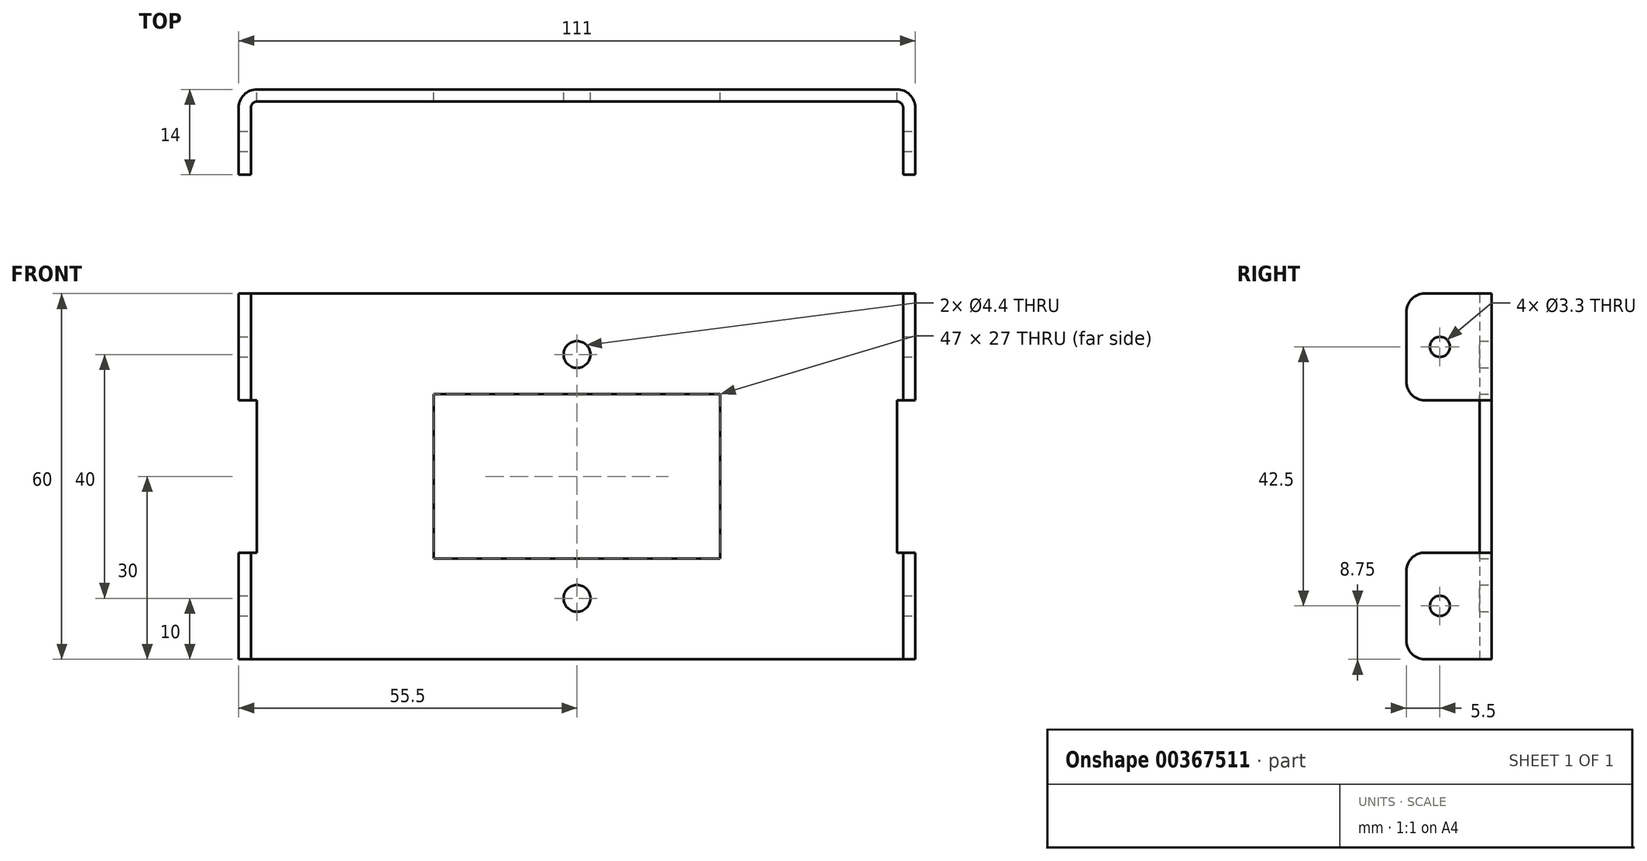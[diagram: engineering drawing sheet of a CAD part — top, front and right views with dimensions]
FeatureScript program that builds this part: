
annotation { "Feature Type Name" : "Feature", "Feature Type Description" : "" }
export const myFeature = defineFeature(function(context is Context, id is Id, definition is map)
    precondition{}
    {
        {
            var Q0;
            Q0=qCreatedBy(makeId("Top.planeOp"),FACE);
            var sketch = newSketch(context, id + "F0", { "sketchPlane" : qUnion([Q0])});
            skLineSegment(sketch, "E0", {"start": v(52.5, 0) * mm, "end": v(-52.5, 0) * mm});
            skLineSegment(sketch, "E1", {"start": v(-53.5, -1) * mm, "end": v(-53.5, -12) * mm});
            skLineSegment(sketch, "E2", {"start": v(53.5, -1) * mm, "end": v(53.5, -12) * mm});
            skPoint(sketch, "E3", {"position": v(0, 0) * mm});
            skPoint(sketch, "E4.visualSharp", {"position": v(-53.5, 0) * mm});
            skArc(sketch, "E4.filletArc", {"start": v(-52.5, 0) * mm, "mid": v(-53.2, -0.3) * mm, "end": v(-53.5, -1) * mm});
            skPoint(sketch, "E5.visualSharp", {"position": v(53.5, 0) * mm});
            skArc(sketch, "E5.filletArc", {"start": v(53.5, -1) * mm, "mid": v(53.2, -0.3) * mm, "end": v(52.5, 0) * mm});
            skLineSegment(sketch, "E6.0", {"start": v(-55.5, -1) * mm, "end": v(-55.5, -12) * mm});
            skLineSegment(sketch, "E6.1", {"start": v(55.5, -1) * mm, "end": v(55.5, -12) * mm});
            skArc(sketch, "E6.2", {"start": v(55.5, -1) * mm, "mid": v(54.62, 1.12) * mm, "end": v(52.5, 2) * mm});
            skLineSegment(sketch, "E6.3", {"start": v(52.5, 2) * mm, "end": v(-52.5, 2) * mm});
            skArc(sketch, "E6.4", {"start": v(-52.5, 2) * mm, "mid": v(-54.62, 1.12) * mm, "end": v(-55.5, -1) * mm});
            skLineSegment(sketch, "E7", {"start": v(-55.5, -12) * mm, "end": v(-53.5, -12) * mm});
            skLineSegment(sketch, "E8", {"start": v(53.5, -12) * mm, "end": v(55.5, -12) * mm});
            skSolve(sketch);
        }
        {
            var Q0;
            Q0=makeQuery(id+"F0.imprint","IMPRINT",FACE,{"disambiguationData":[TD([[makeQuery(id+"F0.imprint","IMPRINT",EDGE,{"derivedFrom":sQuery(id+"F0.wireOp",EDGE,"E0")}),-1.0]])]});
            extrude(context, id + "F1", {"entities" : qUnion([Q0]), "endBound" : BoundingType.SYMMETRIC, "depth" : 60 * mm});
        }
        {
            var Q0;
            Q0=makeQuery(id+"F1.opExtrude","SWEPT_FACE",FACE,{"disambiguationData":[OSD([sQuery(id+"F0.wireOp",EDGE,"E6.3")])]});
            var sketch = newSketch(context, id + "F2", { "sketchPlane" : qUnion([Q0])});
            skLineSegment(sketch, "E9.0", {"start": v(-55.5, 30) * mm, "end": v(-55.5, -30) * mm, "construction": true});
            skLineSegment(sketch, "E10.0", {"start": v(55.5, 30) * mm, "end": v(55.5, -30) * mm, "construction": true});
            skLineSegment(sketch, "E11.bottom", {"start": v(-55.5, 12.5) * mm, "end": v(-52.5, 12.5) * mm});
            skLineSegment(sketch, "E11.top", {"start": v(-55.5, -12.5) * mm, "end": v(-52.5, -12.5) * mm});
            skLineSegment(sketch, "E11.left", {"start": v(-55.5, 12.5) * mm, "end": v(-55.5, -12.5) * mm});
            skLineSegment(sketch, "E11.right", {"start": v(-52.5, 12.5) * mm, "end": v(-52.5, -12.5) * mm});
            skPoint(sketch, "E12", {"position": v(-52.5, 0) * mm});
            skLineSegment(sketch, "E13", {"start": v(0, 0) * mm, "end": v(0, 30) * mm, "construction": true});
            skLineSegment(sketch, "E14.MirrorCS", {"start": v(55.5, 12.5) * mm, "end": v(52.5, 12.5) * mm});
            skLineSegment(sketch, "E15.MirrorCS", {"start": v(55.5, -12.5) * mm, "end": v(52.5, -12.5) * mm});
            skPoint(sketch, "E16.MirrorP", {"position": v(52.5, 0) * mm});
            skLineSegment(sketch, "E17.MirrorCS", {"start": v(55.5, 12.5) * mm, "end": v(55.5, -12.5) * mm});
            skLineSegment(sketch, "E18.MirrorCS", {"start": v(52.5, 12.5) * mm, "end": v(52.5, -12.5) * mm});
            skLineSegment(sketch, "E19.bottom", {"start": v(23.5, 13.5) * mm, "end": v(-23.5, 13.5) * mm});
            skLineSegment(sketch, "E19.top", {"start": v(23.5, -13.5) * mm, "end": v(-23.5, -13.5) * mm});
            skLineSegment(sketch, "E19.left", {"start": v(23.5, 13.5) * mm, "end": v(23.5, -13.5) * mm});
            skLineSegment(sketch, "E19.right", {"start": v(-23.5, 13.5) * mm, "end": v(-23.5, -13.5) * mm});
            skPoint(sketch, "E19.middle", {"position": v(0, 0) * mm});
            skPoint(sketch, "E20", {"position": v(0, 20) * mm});
            skLineSegment(sketch, "E21", {"start": v(0, 0) * mm, "end": v(23.5, 0) * mm, "construction": true});
            skPoint(sketch, "E22", {"position": v(0, -20) * mm});
            skSolve(sketch);
        }
        {
            var Q0;
            Q0=makeQuery(id+"F2.imprint","IMPRINT",FACE,{"disambiguationData":[TD([[makeQuery(id+"F2.imprint","IMPRINT",EDGE,{"derivedFrom":sQuery(id+"F2.wireOp",EDGE,"E11.bottom")}),-1.0]])]});
            var Q1;
            Q1=makeQuery(id+"F2.imprint","IMPRINT",FACE,{"disambiguationData":[TD([[makeQuery(id+"F2.imprint","IMPRINT",EDGE,{"derivedFrom":sQuery(id+"F2.wireOp",EDGE,"E14.MirrorCS")}),1.0]])]});
            var Q2;
            Q2=makeQuery(id+"F2.imprint","IMPRINT",FACE,{"disambiguationData":[TD([[makeQuery(id+"F2.imprint","IMPRINT",EDGE,{"derivedFrom":sQuery(id+"F2.wireOp",EDGE,"E19.bottom")}),1.0]])]});
            extrude(context, id + "F3", {"entities" : qUnion([Q0, Q1, Q2]), "operationType" : NewBodyOperationType.REMOVE, "endBound" : BoundingType.THROUGH_ALL, "oppositeDirection" : true, "depth" : 25 * mm});
        }
        {
            var Q0;
            Q0=sQuery(id+"F2.wireOp",VERTEX,"E20");
            var Q1;
            Q1=sQuery(id+"F2.wireOp",VERTEX,"E22");
            var Q2;
            Q2=makeQuery(id+"F1.opExtrude","SWEPT_BODY",BODY,{"disambiguationData":[OSD([sQuery(id+"F0.wireOp",EDGE,"E0"),sQuery(id+"F0.wireOp",EDGE,"E1"),sQuery(id+"F0.wireOp",EDGE,"E2"),sQuery(id+"F0.wireOp",EDGE,"E4.filletArc"),sQuery(id+"F0.wireOp",EDGE,"E5.filletArc"),sQuery(id+"F0.wireOp",EDGE,"E6.0"),sQuery(id+"F0.wireOp",EDGE,"E6.1"),sQuery(id+"F0.wireOp",EDGE,"E6.2"),sQuery(id+"F0.wireOp",EDGE,"E6.3"),sQuery(id+"F0.wireOp",EDGE,"E6.4"),sQuery(id+"F0.wireOp",EDGE,"E7"),sQuery(id+"F0.wireOp",EDGE,"E8")])]});
            hole(context, id + "F4", {"style" : HoleStyle.SIMPLE, "endStyle" : HoleEndStyle.THROUGH, "standardTappedOrClearance" : lookupTablePath({ "standard" : "ISO", "fit" : "Normal", "size" : "M4", "type" : "Clearance" }), "standardBlindInLast" : lookupTablePath({ "fit" : "Standard", "standard" : "ISO", "size" : "M4", "type" : "Clearance" }), "holeDiameter" : 4.4 * mm, "tappedDepth" : 12 * mm, "tapClearance" : 3, "locations" : qUnion([Q0, Q1]), "scope" : qUnion([Q2])});
        }
        {
            var Q0;
            {var subQ2=sQuery(id+"F0.wireOp",EDGE,"E6.1");Q0=makeQuery(id+"F3.boolean.opBoolean","SPLIT",FACE,{"disambiguationData":[TD([makeQuery(id+"F3.opExtrude","SWEPT_FACE",FACE,{"disambiguationData":[OSD([sQuery(id+"F2.wireOp",EDGE,"E11.bottom")])]})])],"derivedFrom":makeQuery(id+"F1.opExtrude","SWEPT_FACE",FACE,{"disambiguationData":[OSD([subQ2])]})});}
            var sketch = newSketch(context, id + "F5", { "sketchPlane" : qUnion([Q0])});
            skLineSegment(sketch, "E23", {"start": v(-1, 12.5) * mm, "end": v(-12, 30) * mm, "construction": true});
            skLineSegment(sketch, "E24.0.0", {"start": v(-1, -12.5) * mm, "end": v(-12, -12.5) * mm, "construction": true});
            skLineSegment(sketch, "E24.0.1", {"start": v(-12, -12.5) * mm, "end": v(-12, -30) * mm, "construction": true});
            skLineSegment(sketch, "E24.0.2", {"start": v(-12, -30) * mm, "end": v(-1, -30) * mm, "construction": true});
            skLineSegment(sketch, "E24.0.3", {"start": v(-1, -30) * mm, "end": v(-1, -12.5) * mm, "construction": true});
            skLineSegment(sketch, "E25", {"start": v(-1, -30) * mm, "end": v(-12, -12.5) * mm, "construction": true});
            skPoint(sketch, "E26", {"position": v(-6.5, 21.25) * mm});
            skPoint(sketch, "E27", {"position": v(-6.5, -21.25) * mm});
            skSolve(sketch);
        }
        {
            var Q0;
            Q0=sQuery(id+"F5.wireOp",VERTEX,"E26");
            var Q1;
            Q1=sQuery(id+"F5.wireOp",VERTEX,"E27");
            var Q2;
            Q2=makeQuery(id+"F1.opExtrude","SWEPT_BODY",BODY,{"disambiguationData":[OSD([sQuery(id+"F0.wireOp",EDGE,"E0"),sQuery(id+"F0.wireOp",EDGE,"E1"),sQuery(id+"F0.wireOp",EDGE,"E2"),sQuery(id+"F0.wireOp",EDGE,"E4.filletArc"),sQuery(id+"F0.wireOp",EDGE,"E5.filletArc"),sQuery(id+"F0.wireOp",EDGE,"E6.0"),sQuery(id+"F0.wireOp",EDGE,"E6.1"),sQuery(id+"F0.wireOp",EDGE,"E6.2"),sQuery(id+"F0.wireOp",EDGE,"E6.3"),sQuery(id+"F0.wireOp",EDGE,"E6.4"),sQuery(id+"F0.wireOp",EDGE,"E7"),sQuery(id+"F0.wireOp",EDGE,"E8")])]});
            hole(context, id + "F6", {"style" : HoleStyle.SIMPLE, "endStyle" : HoleEndStyle.THROUGH, "standardTappedOrClearance" : lookupTablePath({ "standard" : "ISO", "fit" : "Normal", "size" : "M3", "type" : "Clearance" }), "standardBlindInLast" : lookupTablePath({ "fit" : "Standard", "standard" : "ISO", "size" : "M3", "type" : "Clearance" }), "holeDiameter" : 3.3 * mm, "tappedDepth" : 12 * mm, "tapClearance" : 3, "locations" : qUnion([Q0, Q1]), "scope" : qUnion([Q2])});
        }
        {
            var Q0;
            Q0=makeQuery(id+"F1.opExtrude","CAP_EDGE",EDGE,{"disambiguationData":[OSD([sQuery(id+"F0.wireOp",EDGE,"E7")])],"isStart":false});
            var Q1;
            Q1=makeQuery(id+"F3.boolean.opBoolean","INTERSECT",EDGE,{"derivedFrom":[makeQuery(id+"F1.opExtrude","SWEPT_FACE",FACE,{"disambiguationData":[OSD([sQuery(id+"F0.wireOp",EDGE,"E7")])]}),makeQuery(id+"F3.opExtrude","SWEPT_FACE",FACE,{"disambiguationData":[OSD([sQuery(id+"F2.wireOp",EDGE,"E14.MirrorCS")])]})]});
            var Q2;
            Q2=makeQuery(id+"F3.boolean.opBoolean","INTERSECT",EDGE,{"derivedFrom":[makeQuery(id+"F1.opExtrude","SWEPT_FACE",FACE,{"disambiguationData":[OSD([sQuery(id+"F0.wireOp",EDGE,"E7")])]}),makeQuery(id+"F3.opExtrude","SWEPT_FACE",FACE,{"disambiguationData":[OSD([sQuery(id+"F2.wireOp",EDGE,"E15.MirrorCS")])]})]});
            var Q3;
            Q3=makeQuery(id+"F1.opExtrude","CAP_EDGE",EDGE,{"disambiguationData":[OSD([sQuery(id+"F0.wireOp",EDGE,"E7")])],"isStart":true});
            var Q4;
            Q4=makeQuery(id+"F1.opExtrude","CAP_EDGE",EDGE,{"disambiguationData":[OSD([sQuery(id+"F0.wireOp",EDGE,"E8")])],"isStart":false});
            var Q5;
            Q5=makeQuery(id+"F3.boolean.opBoolean","INTERSECT",EDGE,{"derivedFrom":[makeQuery(id+"F1.opExtrude","SWEPT_FACE",FACE,{"disambiguationData":[OSD([sQuery(id+"F0.wireOp",EDGE,"E8")])]}),makeQuery(id+"F3.opExtrude","SWEPT_FACE",FACE,{"disambiguationData":[OSD([sQuery(id+"F2.wireOp",EDGE,"E11.bottom")])]})]});
            var Q6;
            Q6=makeQuery(id+"F3.boolean.opBoolean","INTERSECT",EDGE,{"derivedFrom":[makeQuery(id+"F1.opExtrude","SWEPT_FACE",FACE,{"disambiguationData":[OSD([sQuery(id+"F0.wireOp",EDGE,"E8")])]}),makeQuery(id+"F3.opExtrude","SWEPT_FACE",FACE,{"disambiguationData":[OSD([sQuery(id+"F2.wireOp",EDGE,"E11.top")])]})]});
            var Q7;
            Q7=makeQuery(id+"F1.opExtrude","CAP_EDGE",EDGE,{"disambiguationData":[OSD([sQuery(id+"F0.wireOp",EDGE,"E8")])],"isStart":true});
            fillet(context, id + "F7", {"entities" : qUnion([Q0, Q1, Q2, Q3, Q4, Q5, Q6, Q7]), "radius" : 3 * mm, "tangentPropagation" : true, "allowEdgeOverflow" : false});
        }
    });
